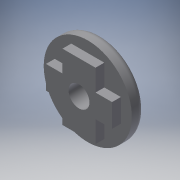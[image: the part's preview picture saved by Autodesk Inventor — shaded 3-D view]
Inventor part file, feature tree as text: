
AUTODESK INVENTOR PART (.ipt)
format: ipt  version: 2016 (Build 200138000, 138)  size: 143,872 bytes
history: native  units: mm
features: other x4, extrude x2, hole x2, fillet x1
ambient origin geometry x8: Origin, YZ Plane, XZ Plane, XY Plane, X Axis, Y Axis, Z Axis, Center Point
bodies: Body1 (feature_tree)
feature tree (9):
  other  "zero_sketch.ipt"
  extrude  "Extrusion1"  Depth=10.0mm
  extrude  "Extrusion2"  Depth=0.6mm TaperAngle=0.0deg
  hole  "Hole1"  [1 undecoded]
  hole  "Hole2"  [1 undecoded]
  fillet  "Fillet1"  Radius=10.0mm
  other  "base+body"
  other  "base+body_1"
  other  "base+body_2"
note: 2 required parameter values undecoded (feature->parameter linkage not recoverable at this tier; creation-order binding heuristic only, values carry confidence <= 0.55)
